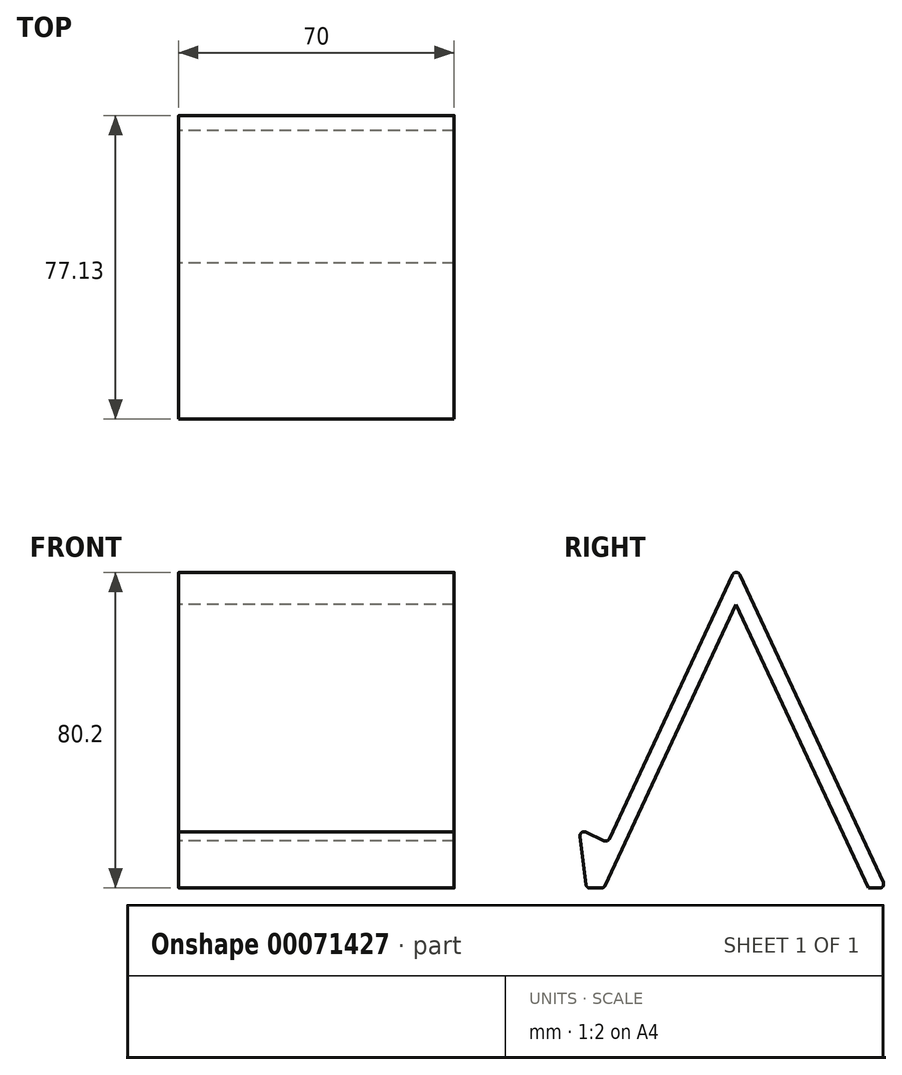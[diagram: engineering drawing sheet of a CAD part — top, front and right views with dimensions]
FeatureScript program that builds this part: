
annotation { "Feature Type Name" : "Feature", "Feature Type Description" : "" }
export const myFeature = defineFeature(function(context is Context, id is Id, definition is map)
    precondition{}
    {
        {
            var Q0;
            Q0=qCreatedBy(makeId("Right.planeOp"),FACE);
            var sketch = newSketch(context, id + "F0", { "sketchPlane" : qUnion([Q0])});
            skLineSegment(sketch, "E0", {"start": v(0, 0) * mm, "end": v(4.41, 0) * mm});
            skLineSegment(sketch, "E1", {"start": v(76.07, 0) * mm, "end": v(38.04, 81.57) * mm});
            skLineSegment(sketch, "E2", {"start": v(38.04, 81.57) * mm, "end": v(5.41, 11.6) * mm});
            skLineSegment(sketch, "E3.0", {"start": v(69.8, 4) * mm, "end": v(38.04, 72.1) * mm});
            skLineSegment(sketch, "E3.2", {"start": v(38.04, 72.1) * mm, "end": v(6.28, 4) * mm});
            skLineSegment(sketch, "E4", {"start": v(0, 0) * mm, "end": v(-1.84, 14.99) * mm});
            skLineSegment(sketch, "E5", {"start": v(-1.84, 14.99) * mm, "end": v(5.41, 11.6) * mm});
            skLineSegment(sketch, "E6", {"start": v(6.28, 4) * mm, "end": v(4.41, 0) * mm});
            skLineSegment(sketch, "E7", {"start": v(69.8, 4) * mm, "end": v(71.66, 0) * mm});
            skLineSegment(sketch, "E8.trimOffspring", {"start": v(71.66, 0) * mm, "end": v(76.07, 0) * mm});
            skSolve(sketch);
        }
        {
            var Q0;
            Q0=makeQuery(id+"F0.imprint","IMPRINT",FACE,{"disambiguationData":[TD([[makeQuery(id+"F0.imprint","IMPRINT",EDGE,{"derivedFrom":sQuery(id+"F0.wireOp",EDGE,"E0")}),1.0]])]});
            extrude(context, id + "F1", {"entities" : qUnion([Q0]), "depth" : 70 * mm});
        }
        {
            var Q0;
            Q0=makeQuery(id+"F1.opExtrude","SWEPT_EDGE",EDGE,{"disambiguationData":[OSD([sQuery(id+"F0.wireOp",EDGE,"E4"),sQuery(id+"F0.wireOp",EDGE,"E5")])]});
            var Q1;
            Q1=makeQuery(id+"F1.opExtrude","SWEPT_EDGE",EDGE,{"disambiguationData":[OSD([sQuery(id+"F0.wireOp",EDGE,"E2"),sQuery(id+"F0.wireOp",EDGE,"E5")])]});
            var Q2;
            Q2=makeQuery(id+"F1.opExtrude","SWEPT_EDGE",EDGE,{"disambiguationData":[OSD([sQuery(id+"F0.wireOp",EDGE,"E1"),sQuery(id+"F0.wireOp",EDGE,"E2")])]});
            var Q3;
            Q3=makeQuery(id+"F1.opExtrude","SWEPT_EDGE",EDGE,{"disambiguationData":[OSD([sQuery(id+"F0.wireOp",EDGE,"E0"),sQuery(id+"F0.wireOp",EDGE,"E1")])]});
            var Q4;
            Q4=makeQuery(id+"F1.opExtrude","SWEPT_EDGE",EDGE,{"disambiguationData":[OSD([sQuery(id+"F0.wireOp",EDGE,"E0"),sQuery(id+"F0.wireOp",EDGE,"E4")])]});
            fillet(context, id + "F2", {"entities" : qUnion([Q0, Q1, Q2, Q3, Q4]), "radius" : 1 * mm, "tangentPropagation" : true, "allowEdgeOverflow" : false});
        }
    });
